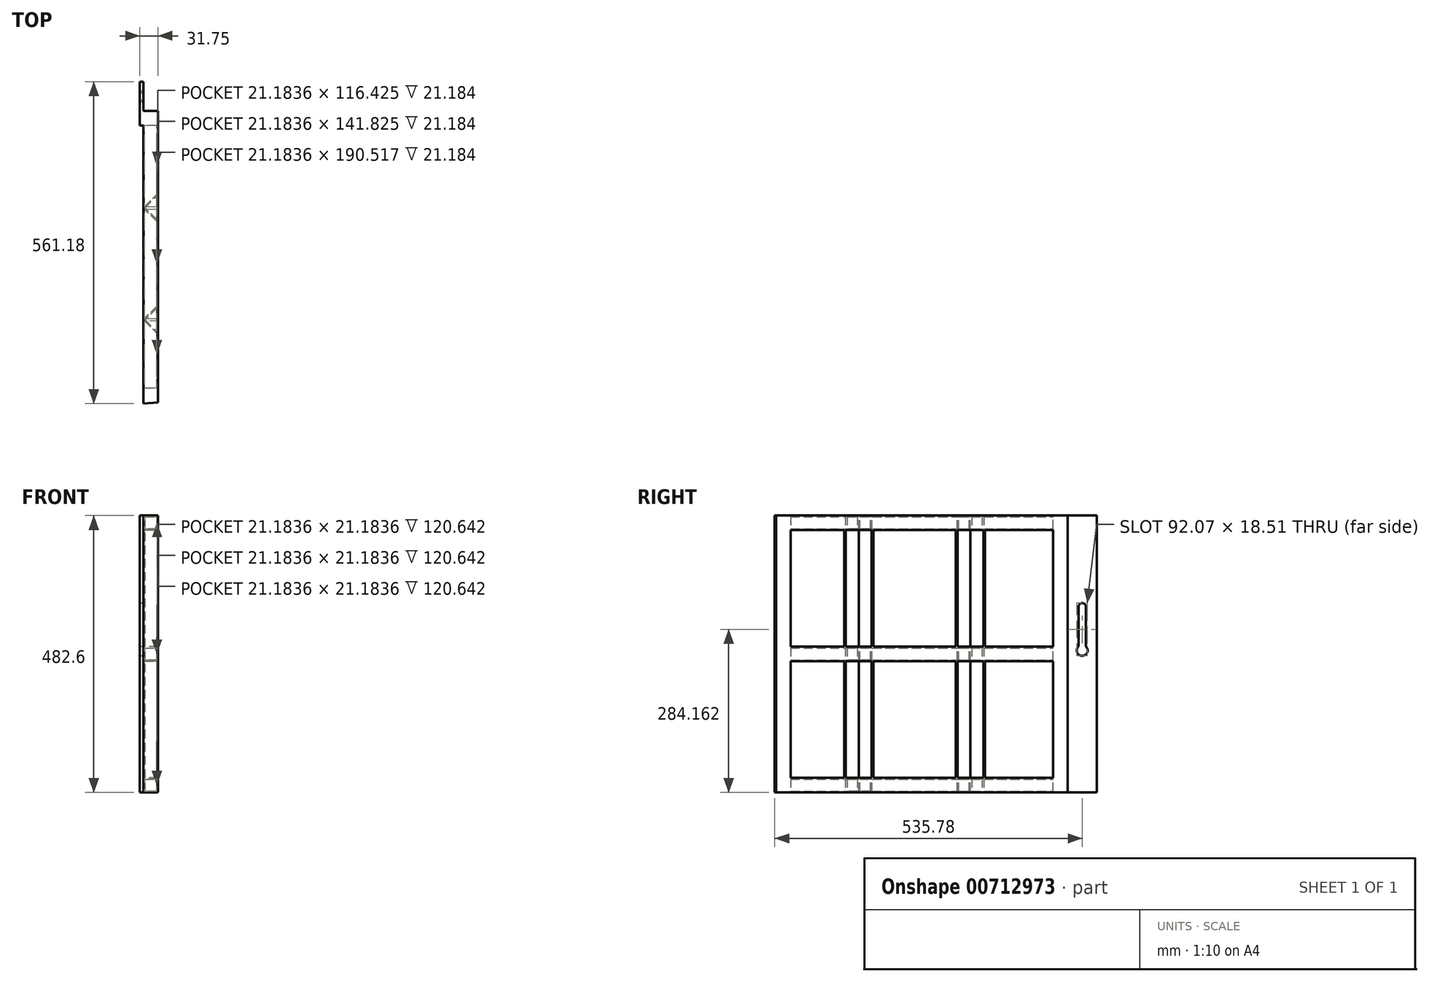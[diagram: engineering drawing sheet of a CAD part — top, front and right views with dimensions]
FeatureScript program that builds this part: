
annotation { "Feature Type Name" : "Feature", "Feature Type Description" : "" }
export const myFeature = defineFeature(function(context is Context, id is Id, definition is map)
    precondition{}
    {
        {
            var Q0;
            Q0=qCreatedBy(makeId("Front.planeOp"),FACE);
            var sketch = newSketch(context, id + "F0", { "sketchPlane" : qUnion([Q0])});
            skLineSegment(sketch, "E0.bottom", {"start": v(-12.7, 12.7) * mm, "end": v(12.7, 12.7) * mm});
            skLineSegment(sketch, "E0.top", {"start": v(-12.7, -12.7) * mm, "end": v(12.7, -12.7) * mm});
            skLineSegment(sketch, "E0.left", {"start": v(-12.7, 12.7) * mm, "end": v(-12.7, -12.7) * mm});
            skLineSegment(sketch, "E0.right", {"start": v(12.7, 12.7) * mm, "end": v(12.7, -12.7) * mm});
            skPoint(sketch, "E0.middle", {"position": v(0, 0) * mm});
            skLineSegment(sketch, "E1.0", {"start": v(-10.6, 10.6) * mm, "end": v(10.6, 10.6) * mm});
            skLineSegment(sketch, "E1.1", {"start": v(-10.6, 10.6) * mm, "end": v(-10.6, -10.6) * mm});
            skLineSegment(sketch, "E1.2", {"start": v(-10.6, -10.6) * mm, "end": v(10.6, -10.6) * mm});
            skLineSegment(sketch, "E1.3", {"start": v(10.6, 10.6) * mm, "end": v(10.6, -10.6) * mm});
            skLineSegment(sketch, "E2.1.0.0", {"start": v(12.7, 241.3) * mm, "end": v(12.7, 215.9) * mm});
            skLineSegment(sketch, "E2.1.0.1", {"start": v(-12.7, 241.3) * mm, "end": v(-12.7, 215.9) * mm});
            skLineSegment(sketch, "E2.1.0.2", {"start": v(-12.7, 215.9) * mm, "end": v(12.7, 215.9) * mm});
            skLineSegment(sketch, "E2.1.0.3", {"start": v(-12.7, 241.3) * mm, "end": v(12.7, 241.3) * mm});
            skLineSegment(sketch, "E2.1.0.4", {"start": v(-10.6, 218) * mm, "end": v(10.6, 218) * mm});
            skPoint(sketch, "E2.1.0.5", {"position": v(0, 228.6) * mm});
            skLineSegment(sketch, "E2.1.0.6", {"start": v(10.6, 239.2) * mm, "end": v(10.6, 218) * mm});
            skLineSegment(sketch, "E2.1.0.7", {"start": v(-10.6, 239.2) * mm, "end": v(10.6, 239.2) * mm});
            skLineSegment(sketch, "E2.1.0.8", {"start": v(-10.6, 239.2) * mm, "end": v(-10.6, 218) * mm});
            skLineSegment(sketch, "E2.2.0.0", {"start": v(12.7, 469.9) * mm, "end": v(12.7, 444.5) * mm});
            skLineSegment(sketch, "E2.2.0.1", {"start": v(-12.7, 469.9) * mm, "end": v(-12.7, 444.5) * mm});
            skLineSegment(sketch, "E2.2.0.2", {"start": v(-12.7, 444.5) * mm, "end": v(12.7, 444.5) * mm});
            skLineSegment(sketch, "E2.2.0.3", {"start": v(-12.7, 469.9) * mm, "end": v(12.7, 469.9) * mm});
            skLineSegment(sketch, "E2.2.0.4", {"start": v(-10.6, 446.6) * mm, "end": v(10.6, 446.6) * mm});
            skPoint(sketch, "E2.2.0.5", {"position": v(0, 457.2) * mm});
            skLineSegment(sketch, "E2.2.0.6", {"start": v(10.6, 467.8) * mm, "end": v(10.6, 446.6) * mm});
            skLineSegment(sketch, "E2.2.0.7", {"start": v(-10.6, 467.8) * mm, "end": v(10.6, 467.8) * mm});
            skLineSegment(sketch, "E2.2.0.8", {"start": v(-10.6, 467.8) * mm, "end": v(-10.6, 446.6) * mm});
            skLineSegment(sketch, "E2.direction1", {"start": v(0, 0) * mm, "end": v(0, 228.6) * mm, "construction": true});
            skSolve(sketch);
        }
        {
            var Q0;
            Q0=makeQuery(id+"F0.imprint","IMPRINT",FACE,{"disambiguationData":[TD([[makeQuery(id+"F0.imprint","IMPRINT",EDGE,{"derivedFrom":sQuery(id+"F0.wireOp",EDGE,"E2.2.0.0")}),-1.0]])]});
            var Q1;
            Q1=makeQuery(id+"F0.imprint","IMPRINT",FACE,{"disambiguationData":[TD([[makeQuery(id+"F0.imprint","IMPRINT",EDGE,{"derivedFrom":sQuery(id+"F0.wireOp",EDGE,"E2.1.0.0")}),-1.0]])]});
            var Q2;
            Q2=makeQuery(id+"F0.imprint","IMPRINT",FACE,{"disambiguationData":[TD([[makeQuery(id+"F0.imprint","IMPRINT",EDGE,{"derivedFrom":sQuery(id+"F0.wireOp",EDGE,"E0.bottom")}),-1.0]])]});
            extrude(context, id + "F1", {"entities" : qUnion([Q0, Q1, Q2]), "depth" : 508 * mm, "offsetDistance" : 25.4 * mm});
        }
        {
            var Q0;
            Q0=makeQuery(id+"F1.opExtrude","SWEPT_FACE",FACE,{"disambiguationData":[OSD([sQuery(id+"F0.wireOp",EDGE,"E2.2.0.3")])]});
            var sketch = newSketch(context, id + "F2", { "sketchPlane" : qUnion([Q0])});
            skLineSegment(sketch, "E3.bottom", {"start": v(12.7, 0) * mm, "end": v(-12.7, 0) * mm});
            skLineSegment(sketch, "E3.top", {"start": v(12.7, -25.4) * mm, "end": v(-12.7, -25.4) * mm});
            skLineSegment(sketch, "E3.left", {"start": v(12.7, 0) * mm, "end": v(12.7, -25.4) * mm});
            skLineSegment(sketch, "E3.right", {"start": v(-12.7, 0) * mm, "end": v(-12.7, -25.4) * mm});
            skLineSegment(sketch, "E4.bottom", {"start": v(-12.7, -508) * mm, "end": v(12.7, -508) * mm});
            skLineSegment(sketch, "E4.top", {"start": v(-12.7, -482.6) * mm, "end": v(12.7, -482.6) * mm});
            skLineSegment(sketch, "E4.left", {"start": v(-12.7, -508) * mm, "end": v(-12.7, -482.6) * mm});
            skLineSegment(sketch, "E4.right", {"start": v(12.7, -508) * mm, "end": v(12.7, -482.6) * mm});
            skSolve(sketch);
        }
        {
            var Q0;
            Q0=makeQuery(id+"F2.imprint","IMPRINT",FACE,{"disambiguationData":[TD([[makeQuery(id+"F2.imprint","IMPRINT",EDGE,{"derivedFrom":sQuery(id+"F2.wireOp",EDGE,"E3.bottom")}),-1.0]])]});
            var Q1;
            Q1=makeQuery(id+"F2.imprint","IMPRINT",FACE,{"disambiguationData":[TD([[makeQuery(id+"F2.imprint","IMPRINT",EDGE,{"derivedFrom":sQuery(id+"F2.wireOp",EDGE,"E4.bottom")}),1.0]])]});
            extrude(context, id + "F3", {"entities" : qUnion([Q0, Q1]), "operationType" : NewBodyOperationType.ADD, "oppositeDirection" : true, "depth" : 482.6 * mm, "offsetDistance" : 25.4 * mm});
        }
        {
            var Q0;
            Q0=makeQuery(id+"F3.boolean.opBoolean","MERGE",FACE,{"derivedFrom":[makeQuery(id+"F1.opExtrude","SWEPT_FACE",FACE,{"disambiguationData":[OSD([sQuery(id+"F0.wireOp",EDGE,"E0.left")])]}),makeQuery(id+"F1.opExtrude","SWEPT_FACE",FACE,{"disambiguationData":[OSD([sQuery(id+"F0.wireOp",EDGE,"E2.1.0.1")])]}),makeQuery(id+"F1.opExtrude","SWEPT_FACE",FACE,{"disambiguationData":[OSD([sQuery(id+"F0.wireOp",EDGE,"E2.2.0.1")])]}),makeQuery(id+"F3.opExtrude","SWEPT_FACE",FACE,{"disambiguationData":[OSD([sQuery(id+"F2.wireOp",EDGE,"E3.right")])]}),makeQuery(id+"F3.opExtrude","SWEPT_FACE",FACE,{"disambiguationData":[OSD([sQuery(id+"F2.wireOp",EDGE,"E4.left")])]})]});
            var sketch = newSketch(context, id + "F4", { "sketchPlane" : qUnion([Q0])});
            skLineSegment(sketch, "E5.bottom", {"start": v(-50.8, -12.7) * mm, "end": v(25.4, -12.7) * mm});
            skLineSegment(sketch, "E5.top", {"start": v(-50.8, 469.9) * mm, "end": v(25.4, 469.9) * mm});
            skLineSegment(sketch, "E5.left", {"start": v(-50.8, -12.7) * mm, "end": v(-50.8, 469.9) * mm});
            skLineSegment(sketch, "E5.right", {"start": v(25.4, -12.7) * mm, "end": v(25.4, 469.9) * mm});
            skArc(sketch, "E6", {"start": v(-31.75, 242.05) * mm, "mid": v(-25.4, 225.43) * mm, "end": v(-19.05, 242.05) * mm});
            skArc(sketch, "E7", {"start": v(-19.05, 311.15) * mm, "mid": v(-25.4, 317.5) * mm, "end": v(-31.75, 311.15) * mm});
            skLineSegment(sketch, "E8", {"start": v(-31.75, 311.15) * mm, "end": v(-31.75, 242.05) * mm});
            skLineSegment(sketch, "E9", {"start": v(-19.05, 311.15) * mm, "end": v(-19.05, 242.05) * mm});
            skSolve(sketch);
        }
        {
            var Q0;
            Q0 = qSketchRegion(id + "F4", true);
            extrude(context, id + "F5", {"entities" : qUnion([Q0]), "operationType" : NewBodyOperationType.ADD, "depth" : 6.35 * mm, "offsetDistance" : 25.4 * mm});
        }
        {
            var Q0;
            Q0=makeQuery(id+"F5.boolean.opBoolean","MERGE",FACE,{"derivedFrom":[makeQuery(id+"F1.opExtrude","SWEPT_FACE",FACE,{"disambiguationData":[OSD([sQuery(id+"F0.wireOp",EDGE,"E2.2.0.3")])]}),makeQuery(id+"F5.opExtrude","SWEPT_FACE",FACE,{"disambiguationData":[OSD([sQuery(id+"F4.wireOp",EDGE,"E5.top")])]})]});
            var sketch = newSketch(context, id + "F6", { "sketchPlane" : qUnion([Q0])});
            skLineSegment(sketch, "E10", {"start": v(12.7, -194.73) * mm, "end": v(-12.7, -169.33) * mm});
            skLineSegment(sketch, "E11", {"start": v(-12.7, -169.33) * mm, "end": v(12.7, -143.93) * mm});
            skLineSegment(sketch, "E12.0", {"start": v(-9.72, -169.33) * mm, "end": v(12.7, -146.91) * mm});
            skLineSegment(sketch, "E12.1", {"start": v(12.7, -191.75) * mm, "end": v(-9.72, -169.33) * mm});
            skLineSegment(sketch, "E13", {"start": v(12.7, -194.73) * mm, "end": v(12.7, -191.75) * mm});
            skLineSegment(sketch, "E14", {"start": v(12.7, -143.93) * mm, "end": v(12.7, -146.91) * mm});
            skLineSegment(sketch, "E15", {"start": v(-12.7, -266.7) * mm, "end": v(12.7, -266.7) * mm, "construction": true});
            skLineSegment(sketch, "E16.MirrorCS", {"start": v(12.7, -389.47) * mm, "end": v(12.7, -386.49) * mm});
            skLineSegment(sketch, "E17.MirrorCS", {"start": v(12.7, -338.67) * mm, "end": v(12.7, -341.65) * mm});
            skLineSegment(sketch, "E18.MirrorCS", {"start": v(-12.7, -364.07) * mm, "end": v(12.7, -389.47) * mm});
            skLineSegment(sketch, "E19.MirrorCS", {"start": v(-9.72, -364.07) * mm, "end": v(12.7, -386.49) * mm});
            skLineSegment(sketch, "E20.MirrorCS", {"start": v(12.7, -338.67) * mm, "end": v(-12.7, -364.07) * mm});
            skLineSegment(sketch, "E21.MirrorCS", {"start": v(12.7, -341.65) * mm, "end": v(-9.72, -364.07) * mm});
            skSolve(sketch);
        }
        {
            var Q0;
            Q0 = qSketchRegion(id + "F6", true);
            extrude(context, id + "F7", {"entities" : qUnion([Q0]), "operationType" : NewBodyOperationType.ADD, "oppositeDirection" : true, "depth" : 482.6 * mm, "offsetDistance" : 25.4 * mm});
        }
        {
            var Q0;
            Q0=makeQuery(id+"F5.boolean.opBoolean","MERGE",FACE,{"derivedFrom":[makeQuery(id+"F1.opExtrude","SWEPT_FACE",FACE,{"disambiguationData":[OSD([sQuery(id+"F0.wireOp",EDGE,"E2.2.0.3")])]}),makeQuery(id+"F5.opExtrude","SWEPT_FACE",FACE,{"disambiguationData":[OSD([sQuery(id+"F4.wireOp",EDGE,"E5.top")])]})]});
            var sketch = newSketch(context, id + "F8", { "sketchPlane" : qUnion([Q0])});
            skLineSegment(sketch, "E22", {"start": v(12.7, -508) * mm, "end": v(-12.7, -510.38) * mm});
            skLineSegment(sketch, "E23", {"start": v(-12.7, -510.38) * mm, "end": v(-12.7, -508) * mm});
            skLineSegment(sketch, "E24", {"start": v(-12.7, -508) * mm, "end": v(12.7, -508) * mm});
            skSolve(sketch);
        }
        {
            var Q0;
            Q0=makeQuery(id+"F8.imprint","IMPRINT",FACE,{"disambiguationData":[TD([[makeQuery(id+"F8.imprint","IMPRINT",EDGE,{"derivedFrom":sQuery(id+"F8.wireOp",EDGE,"E22")}),-1.0]])]});
            extrude(context, id + "F9", {"entities" : qUnion([Q0]), "operationType" : NewBodyOperationType.ADD, "oppositeDirection" : true, "depth" : 482.6 * mm, "offsetDistance" : 25.4 * mm});
        }
    });
